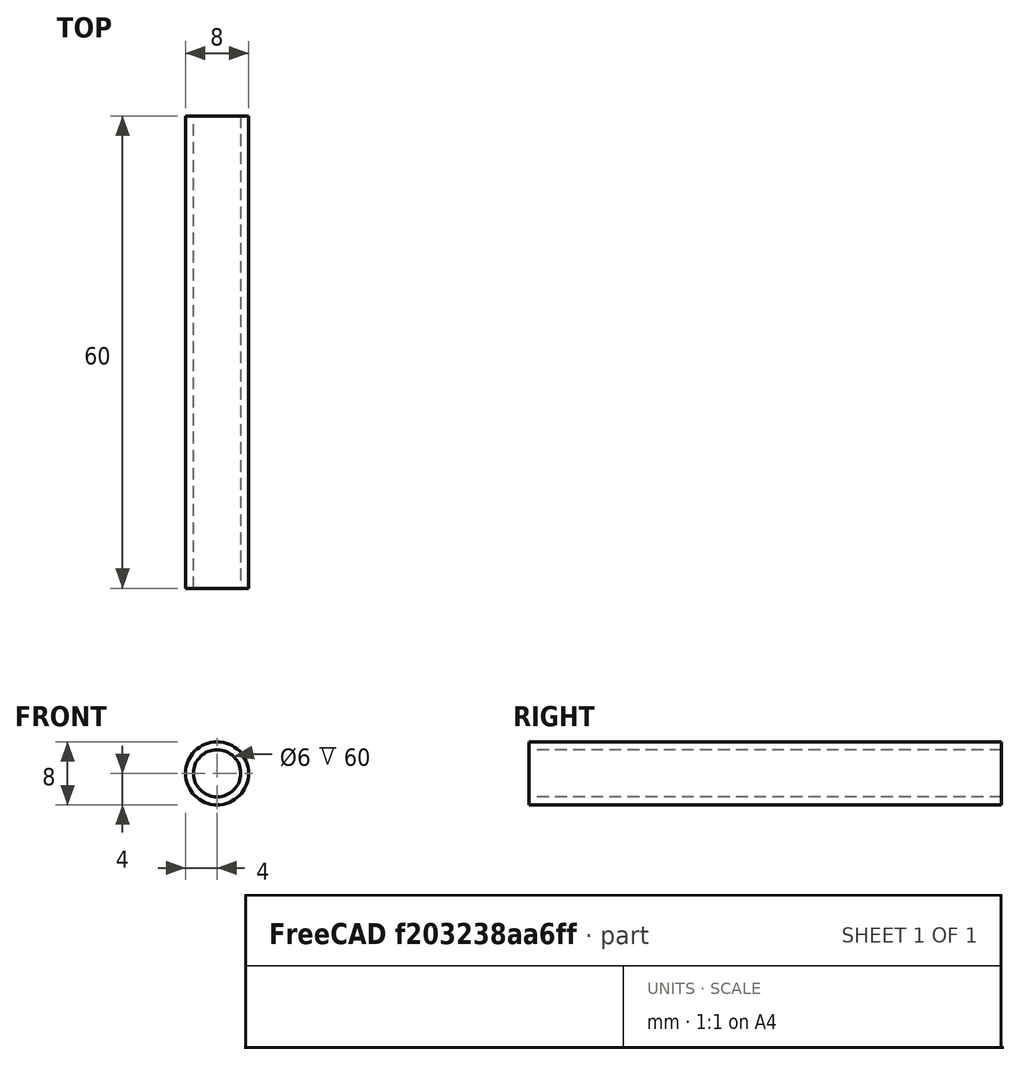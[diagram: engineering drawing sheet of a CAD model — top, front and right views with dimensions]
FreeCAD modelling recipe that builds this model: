
FCSTD DOCUMENT  (FreeCAD 0.18R16146 (Git))
Label: tube
Comment: # 2020-08-04 16:30:14: read from <userpath>/repositories/sussex_neuro/Olfactometer/hardware/mechanics/from_raiser_et_al/tube.ipt
License: All rights reserved
LicenseURL: http://en.wikipedia.org/wiki/All_rights_reserved
objects: Sketcher::SketchObject×2, Spreadsheet::Sheet×1, Part::Extrusion×1
note: 3 computed .brp shape members not serialized (recipe doc carries the construction recipe); baked Part::Feature solids carry a one-line shape summary decoded from their .brp

FEATURE [Spreadsheet::Sheet] Parameters
  cells = A1=Parameter; B1=Value; C1=Fromula; D1=Tolerance; E1=Comment; A2=d10; B2(d10_)=0.3; C2=0.3mm; D2=NOMINAL; A3=d11; B3(d11_)=0.3; C3=0.3mm; D3=NOMINAL; A4=d12; B4(d12_)=0.5; C4=0.5mm; D4=NOMINAL; A5=d13; B5(d13_)=2; C5=2mm; D5=NOMINAL; A6=d14; B6(d14_)=0; C6=0mm; D6=NOMINAL; A7=d15; B7(d15_)=20; C7=20mm; D7=NOMINAL; A8=d4; B8(d4_)=8; C8=8mm; D8=NOMINAL; A9=d6; B9(d6_)=6.000000000000001; C9=6mm; D9=NOMINAL; A10=d7; B10(d7_)=60; C10=60mm; D10=NOMINAL; A11=d8; B11(d8_)=0; C11=0°; D11=NOMINAL; A12=d9; B12(d9_)=0.3; C12=0.3mm; D12=NOMINAL
FEATURE [Sketcher::SketchObject] Sketch3
  Placement = pos=(0,0,0) rot=(0,0.707107,0.707107;3.14159rad)
  sketch-geometry (2):
    g0: Circle CenterX=0 CenterY=0 CenterZ=0 NormalX=0 NormalY=0 NormalZ=1 AngleXU=0 Radius=4
    g1: Circle CenterX=0 CenterY=0 CenterZ=0 NormalX=0 NormalY=0 NormalZ=1 AngleXU=0 Radius=3
  constraints (2):
    c: Radius(g0) = 4  'd4'
    c: Radius(g1) = 3  'd6'
FEATURE [Sketcher::SketchObject] Sketch3_bp
  Placement = pos=(0,0,0) rot=(0,0.707107,0.707107;3.14159rad)
  sketch-geometry (2):
    g0: Circle CenterX=0 CenterY=0 CenterZ=0 NormalX=0 NormalY=0 NormalZ=1 AngleXU=0 Radius=4
    g1: Circle CenterX=0 CenterY=0 CenterZ=0 NormalX=0 NormalY=0 NormalZ=1 AngleXU=0 Radius=3
FEATURE [Part::Extrusion] Extrusion2
  Base = -> Sketch3_bp
  Dir = (0,1,0)
  DirMode = 0
  FaceMakerClass = Part::FaceMakerBullseye
  LengthFwd = 60
  LengthRev = 0
  Solid = true
  Symmetric = false
  expr: LengthFwd = Parameters.d7_
  expr: TaperAngle = Parameters.d8_
